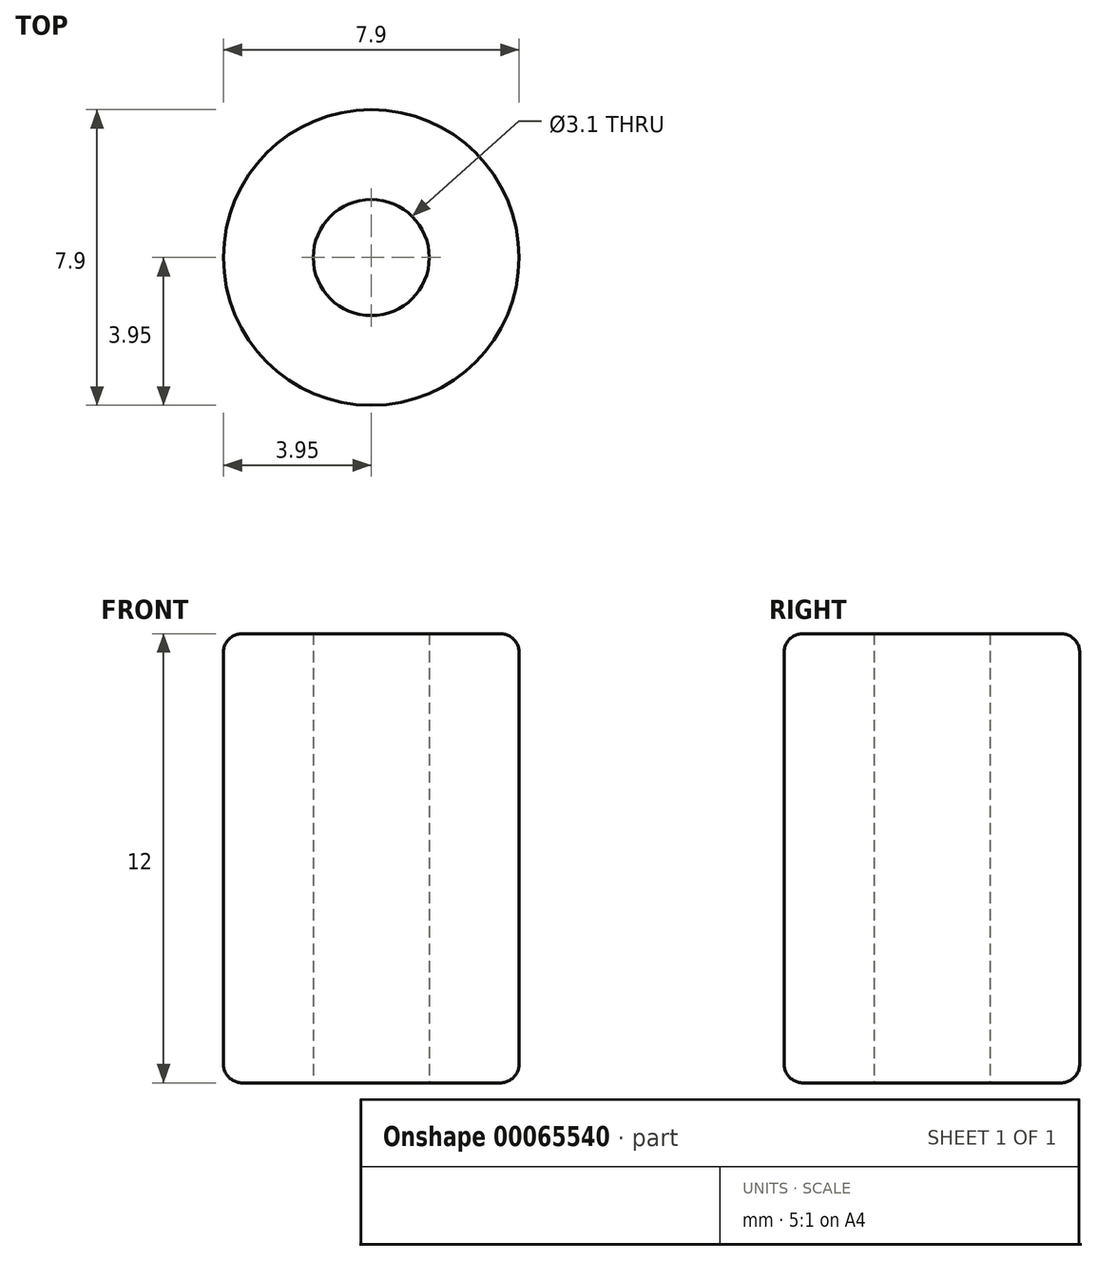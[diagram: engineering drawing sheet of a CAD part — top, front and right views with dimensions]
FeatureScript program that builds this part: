
annotation { "Feature Type Name" : "Feature", "Feature Type Description" : "" }
export const myFeature = defineFeature(function(context is Context, id is Id, definition is map)
    precondition{}
    {
        {
            var Q0;
            Q0=qCreatedBy(makeId("Top.planeOp"),FACE);
            var sketch = newSketch(context, id + "F0", { "sketchPlane" : qUnion([Q0])});
            skCircle(sketch, "E0", {"center": v(0, 0) * mm, "radius": 3.95 * mm});
            skSolve(sketch);
        }
        {
            var Q0;
            Q0=makeQuery(id+"F0.imprint","IMPRINT",FACE,{"disambiguationData":[TD([[makeQuery(id+"F0.imprint","IMPRINT",EDGE,{"derivedFrom":sQuery(id+"F0.wireOp",EDGE,"E0")}),1.0]])]});
            extrude(context, id + "F1", {"entities" : qUnion([Q0]), "depth" : 12 * mm});
        }
        {
            var Q0;
            Q0=makeQuery(id+"F1.opExtrude","CAP_FACE",FACE,{"disambiguationData":[OSD([sQuery(id+"F0.wireOp",EDGE,"E0")])],"isStart":true});
            var sketch = newSketch(context, id + "F2", { "sketchPlane" : qUnion([Q0])});
            skCircle(sketch, "E1", {"center": v(0, 0) * mm, "radius": 1.55 * mm});
            skSolve(sketch);
        }
        {
            var Q0;
            Q0=makeQuery(id+"F2.imprint","IMPRINT",FACE,{"disambiguationData":[TD([[makeQuery(id+"F2.imprint","IMPRINT",EDGE,{"derivedFrom":sQuery(id+"F2.wireOp",EDGE,"E1")}),1.0]])]});
            extrude(context, id + "F3", {"entities" : qUnion([Q0]), "operationType" : NewBodyOperationType.REMOVE, "endBound" : BoundingType.THROUGH_ALL, "oppositeDirection" : true, "depth" : 25 * mm});
        }
        {
            var Q0;
            Q0=makeQuery(id+"F1.opExtrude","CAP_EDGE",EDGE,{"disambiguationData":[OSD([sQuery(id+"F0.wireOp",EDGE,"E0")])],"isStart":true});
            var Q1;
            Q1=makeQuery(id+"F1.opExtrude","CAP_EDGE",EDGE,{"disambiguationData":[OSD([sQuery(id+"F0.wireOp",EDGE,"E0")])],"isStart":false});
            fillet(context, id + "F4", {"entities" : qUnion([Q0, Q1]), "radius" : .5 * mm, "tangentPropagation" : true, "allowEdgeOverflow" : false});
        }
    });
